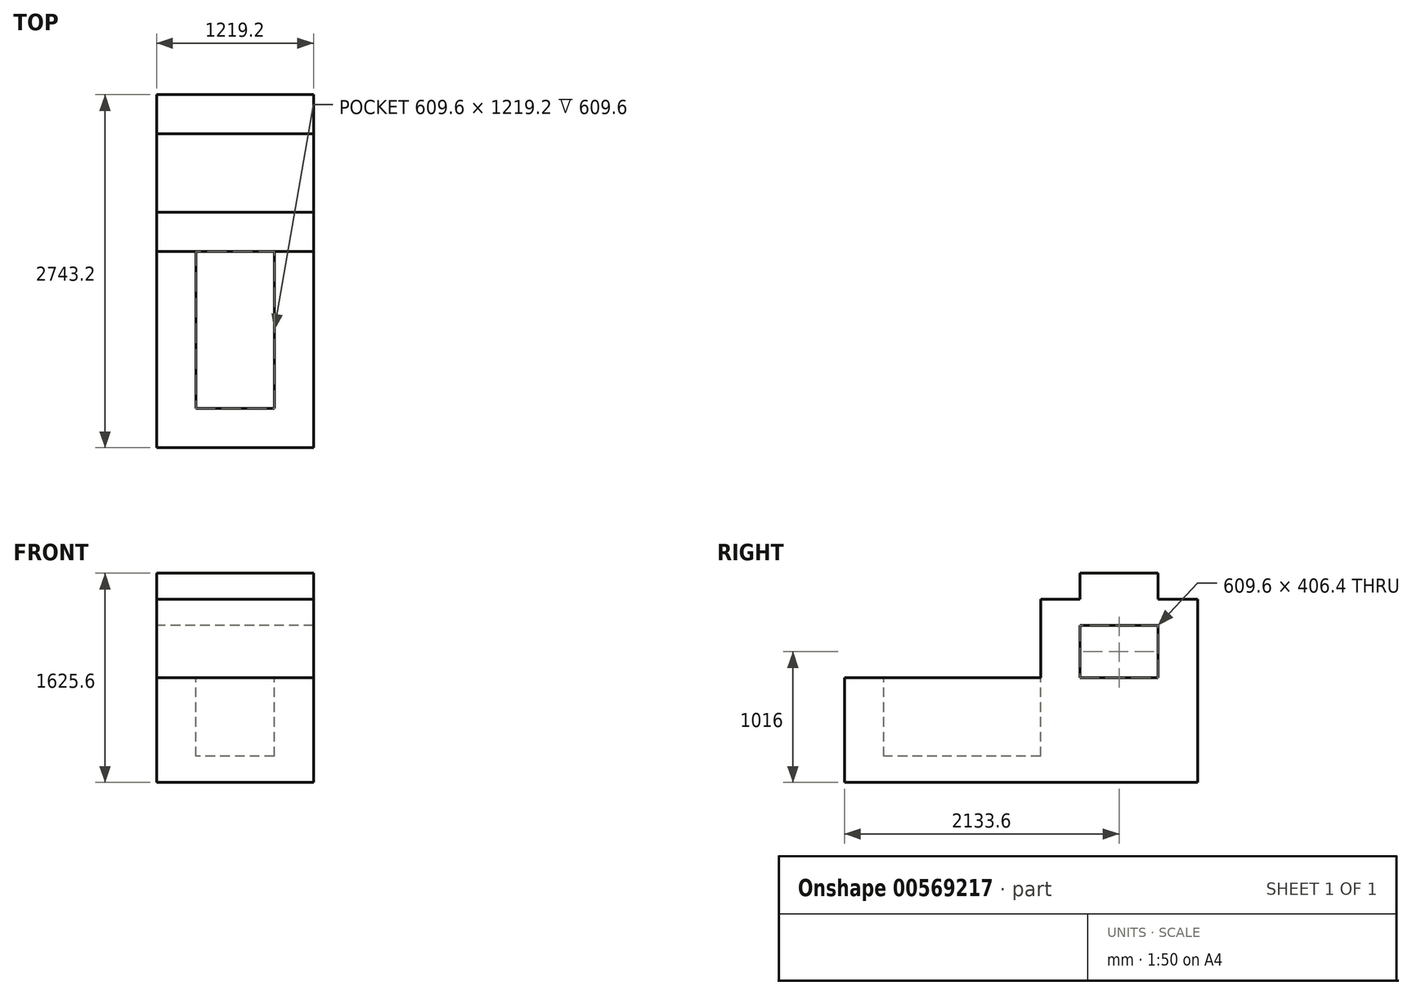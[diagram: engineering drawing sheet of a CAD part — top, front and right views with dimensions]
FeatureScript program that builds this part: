
annotation { "Feature Type Name" : "Feature", "Feature Type Description" : "" }
export const myFeature = defineFeature(function(context is Context, id is Id, definition is map)
    precondition{}
    {
        {
            var Q0;
            Q0=qCreatedBy(makeId("Right.planeOp"),FACE);
            var sketch = newSketch(context, id + "F0", { "sketchPlane" : qUnion([Q0])});
            skLineSegment(sketch, "E0", {"start": v(-8635.06, -1485.55) * mm, "end": v(-5891.86, -1485.55) * mm});
            skLineSegment(sketch, "E1", {"start": v(-5891.86, -1485.55) * mm, "end": v(-5891.86, -63.15) * mm});
            skLineSegment(sketch, "E2", {"start": v(-5891.86, -63.15) * mm, "end": v(-6196.66, -63.15) * mm});
            skLineSegment(sketch, "E3", {"start": v(-6196.66, -63.15) * mm, "end": v(-6196.66, 140.05) * mm});
            skLineSegment(sketch, "E4", {"start": v(-6196.66, 140.05) * mm, "end": v(-6806.26, 140.05) * mm});
            skLineSegment(sketch, "E5", {"start": v(-6806.26, 140.05) * mm, "end": v(-6806.26, -63.15) * mm});
            skLineSegment(sketch, "E6", {"start": v(-6806.26, -63.15) * mm, "end": v(-7111.06, -63.15) * mm});
            skLineSegment(sketch, "E7", {"start": v(-7111.06, -63.15) * mm, "end": v(-7111.06, -672.75) * mm});
            skLineSegment(sketch, "E8", {"start": v(-7111.06, -672.75) * mm, "end": v(-8635.06, -672.75) * mm});
            skLineSegment(sketch, "E9", {"start": v(-8635.06, -672.75) * mm, "end": v(-8635.06, -1485.55) * mm});
            skLineSegment(sketch, "E10", {"start": v(-6806.26, -672.75) * mm, "end": v(-6196.66, -672.75) * mm});
            skLineSegment(sketch, "E11", {"start": v(-6196.66, -672.75) * mm, "end": v(-6196.66, -266.35) * mm});
            skLineSegment(sketch, "E12", {"start": v(-6196.66, -266.35) * mm, "end": v(-6806.26, -266.35) * mm});
            skLineSegment(sketch, "E13", {"start": v(-6806.26, -266.35) * mm, "end": v(-6806.26, -672.75) * mm});
            skSolve(sketch);
        }
        {
            var Q0;
            Q0 = qSketchRegion(id + "F0", true);
            extrude(context, id + "F1", {"entities" : qUnion([Q0]), "depth" : 1219.2 * mm, "offsetDistance" : 25.4 * mm});
        }
        {
            var Q0;
            Q0=makeQuery(id+"F1.opExtrude","SWEPT_FACE",FACE,{"disambiguationData":[OSD([sQuery(id+"F0.wireOp",EDGE,"E8")])]});
            var sketch = newSketch(context, id + "F2", { "sketchPlane" : qUnion([Q0])});
            skLineSegment(sketch, "E14", {"start": v(914.4, -7111.06) * mm, "end": v(914.4, -8330.26) * mm});
            skLineSegment(sketch, "E15", {"start": v(914.4, -8330.26) * mm, "end": v(304.8, -8330.26) * mm});
            skLineSegment(sketch, "E16", {"start": v(304.8, -8330.26) * mm, "end": v(304.8, -7111.06) * mm});
            skSolve(sketch);
        }
        {
            var Q0;
            {var subQ0=sQuery(id+"F2.wireOp",EDGE,"E14");Q0=makeQuery(id+"F2.imprint","IMPRINT",FACE,{"disambiguationData":[TD([[makeQuery(id+"F2.imprint","IMPRINT",EDGE,{"derivedFrom":subQ0}),-1.0]])]});}
            extrude(context, id + "F3", {"entities" : qUnion([Q0]), "operationType" : NewBodyOperationType.REMOVE, "oppositeDirection" : true, "depth" : 609.6 * mm, "offsetDistance" : 25.4 * mm});
        }
    });
